# Revit family: No interlocked sockets 24_42 V
name_source: partatom
category: Installations électriques
revit_build: Autodesk Revit 2018 (Build: 20170223_1515(x64)
units: mm (PartAtom-declared; Revit-internal decimal feet)

## family parameters
Conserver l'orientation des annotations = Non
Cote de connecteur circulaire = Utiliser le diamètre
Couper avec des vides une fois chargée = Non
Hôte = Face
Partagée = Non
Point de calcul de pièce = Non
Type d'élément = Normal

## types (3) — shared parameters
Elévation par défaut = 1000 mm  [stored 3.28084 ft]
Fabricant = LEGRAND
International standard socket for flush mounting or surface mounting with accessory allows the connection of power devices = International standard socket for flush mounting or surface mounting with accessory allows the connection of power devices
Maximum use temperature = 40
Minimum use temperature = -25
Number of poles = 2
Position of earth h = 12
Product family = 0854-P17 TEMPRA PRO
Standard IEC or NFC = IEC
Tension V = 40 50 V  50/60 Hz white
characteristic color = white
connecting type = screw terminals
halogen free = Oui
material of box = plastic
protection class IP = IP44
resistance to chocks IK = 9

## per-type parameters (varying)
| type | Description | Flush E or Surface mounting S | depth for flush mounting mm | depth mm | height mm | horizontal fixing distance mm | intensity A | vertical fixing distance mm | width mm |
| P17 - 2P - 16A | LG-057350_Table base 2P 16A 24/42V | flush and surface mounting | 33 mm  [stored 0.108268 ft] | 66 mm | 84 mm | 70 mm  [stored 0.229659 ft] | 16 A | 70 mm  [stored 0.229659 ft] | 84 mm |
| P17 - 2P - 32A - ELV 1 | LG-055297_Table base 2P 32A 42V ELV | flush and surface mounting | 33 mm  [stored 0.108268 ft] | 66 mm | 84 mm | 70 mm  [stored 0.229659 ft] | 32 A | 70 mm  [stored 0.229659 ft] | 84 mm |
| P17 - 2P - 32A - ELV | LG-055265_ELV 2P 32A 24/42V | flush mounting | 23 mm | 60 mm  [stored 0.19685 ft] | 76 mm | 42 mm | 32 A | 42 mm | 55 mm  [stored 0.180446 ft] |

note: [stored X ft] marks values corroborated as IEEE doubles in the binary element streams (Revit-internal decimal feet)
